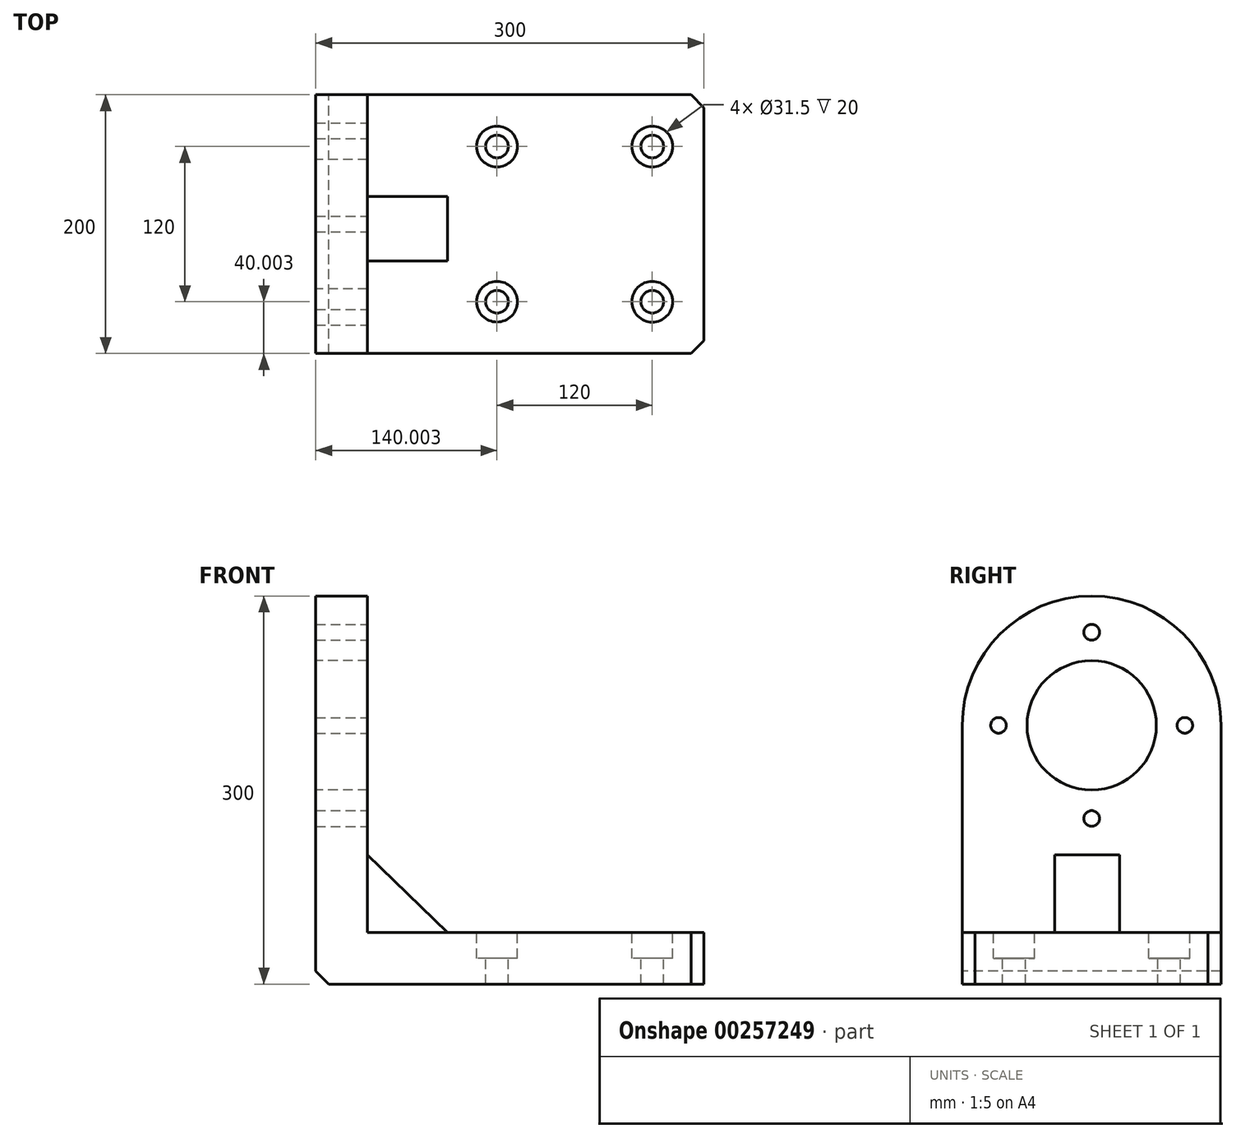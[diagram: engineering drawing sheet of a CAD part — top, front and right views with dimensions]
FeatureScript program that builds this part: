
annotation { "Feature Type Name" : "Feature", "Feature Type Description" : "" }
export const myFeature = defineFeature(function(context is Context, id is Id, definition is map)
    precondition{}
    {
        {
            var Q0;
            Q0=qCreatedBy(makeId("Top.planeOp"),FACE);
            var sketch = newSketch(context, id + "F0", { "sketchPlane" : qUnion([Q0])});
            skLineSegment(sketch, "E0.bottom", {"start": v(-159.08, 103.5) * mm, "end": v(140.92, 103.5) * mm});
            skLineSegment(sketch, "E0.top", {"start": v(-159.08, -96.5) * mm, "end": v(140.92, -96.5) * mm});
            skLineSegment(sketch, "E0.left", {"start": v(-159.08, 103.5) * mm, "end": v(-159.08, -96.5) * mm});
            skLineSegment(sketch, "E0.right", {"start": v(140.92, 103.5) * mm, "end": v(140.92, -96.5) * mm});
            skSolve(sketch);
        }
        {
            var Q0;
            Q0 = qSketchRegion(id + "F0", true);
            extrude(context, id + "F1", {"entities" : qUnion([Q0]), "depth" : 40 * mm});
        }
        {
            var Q0;
            Q0=makeQuery(id+"F1.opExtrude","CAP_FACE",FACE,{"disambiguationData":[OSD([sQuery(id+"F0.wireOp",EDGE,"E0.bottom"),sQuery(id+"F0.wireOp",EDGE,"E0.top"),sQuery(id+"F0.wireOp",EDGE,"E0.left"),sQuery(id+"F0.wireOp",EDGE,"E0.right")])],"isStart":false});
            var sketch = newSketch(context, id + "F2", { "sketchPlane" : qUnion([Q0])});
            skCircle(sketch, "E1", {"center": v(100.92, 63.5) * mm, "radius": 15.75 * mm});
            skCircle(sketch, "E2", {"center": v(100.92, -56.5) * mm, "radius": 15.75 * mm});
            skCircle(sketch, "E3", {"center": v(-19.08, 63.5) * mm, "radius": 15.75 * mm});
            skCircle(sketch, "E4", {"center": v(-19.08, -56.5) * mm, "radius": 15.75 * mm});
            skSolve(sketch);
        }
        {
            var Q0;
            Q0 = qSketchRegion(id + "F2", true);
            extrude(context, id + "F3", {"entities" : qUnion([Q0]), "operationType" : NewBodyOperationType.REMOVE, "oppositeDirection" : true, "depth" : 20 * mm});
        }
        {
            var Q0;
            Q0=makeQuery(id+"F1.opExtrude","CAP_FACE",FACE,{"disambiguationData":[OSD([sQuery(id+"F0.wireOp",EDGE,"E0.bottom"),sQuery(id+"F0.wireOp",EDGE,"E0.top"),sQuery(id+"F0.wireOp",EDGE,"E0.left"),sQuery(id+"F0.wireOp",EDGE,"E0.right")])],"isStart":false});
            var sketch = newSketch(context, id + "F4", { "sketchPlane" : qUnion([Q0])});
            skCircle(sketch, "E5", {"center": v(-19.08, 63.5) * mm, "radius": 8.75 * mm});
            skCircle(sketch, "E6", {"center": v(100.92, 63.5) * mm, "radius": 8.75 * mm});
            skCircle(sketch, "E7", {"center": v(-19.08, -56.5) * mm, "radius": 8.75 * mm});
            skCircle(sketch, "E8", {"center": v(100.92, -56.5) * mm, "radius": 8.75 * mm});
            skSolve(sketch);
        }
        {
            var Q0;
            Q0 = qSketchRegion(id + "F4", true);
            extrude(context, id + "F5", {"entities" : qUnion([Q0]), "operationType" : NewBodyOperationType.REMOVE, "endBound" : BoundingType.THROUGH_ALL, "oppositeDirection" : true, "depth" : 25.4 * mm});
        }
        {
            var Q0;
            Q0=makeQuery(id+"F1.opExtrude","CAP_FACE",FACE,{"disambiguationData":[OSD([sQuery(id+"F0.wireOp",EDGE,"E0.bottom"),sQuery(id+"F0.wireOp",EDGE,"E0.top"),sQuery(id+"F0.wireOp",EDGE,"E0.left"),sQuery(id+"F0.wireOp",EDGE,"E0.right")])],"isStart":false});
            var sketch = newSketch(context, id + "F6", { "sketchPlane" : qUnion([Q0])});
            skLineSegment(sketch, "E9.bottom", {"start": v(-159.08, 103.5) * mm, "end": v(-119.08, 103.5) * mm});
            skLineSegment(sketch, "E9.top", {"start": v(-159.08, -96.5) * mm, "end": v(-119.08, -96.5) * mm});
            skLineSegment(sketch, "E9.left", {"start": v(-159.08, 103.5) * mm, "end": v(-159.08, -96.5) * mm});
            skLineSegment(sketch, "E9.right", {"start": v(-119.08, 103.5) * mm, "end": v(-119.08, -96.5) * mm});
            skSolve(sketch);
        }
        {
            var Q0;
            Q0 = qSketchRegion(id + "F6", true);
            extrude(context, id + "F7", {"entities" : qUnion([Q0]), "operationType" : NewBodyOperationType.ADD, "depth" : 260 * mm});
        }
        {
            var Q0;
            Q0=makeQuery(id+"F7.boolean.opBoolean","MERGE",FACE,{"derivedFrom":[makeQuery(id+"F1.opExtrude","SWEPT_FACE",FACE,{"disambiguationData":[OSD([sQuery(id+"F0.wireOp",EDGE,"E0.left")])]}),makeQuery(id+"F7.opExtrude","SWEPT_FACE",FACE,{"disambiguationData":[OSD([sQuery(id+"F6.wireOp",EDGE,"E9.left")])]})]});
            var sketch = newSketch(context, id + "F8", { "sketchPlane" : qUnion([Q0])});
            skCircle(sketch, "E10", {"center": v(-3.5, 200) * mm, "radius": 100 * mm});
            skPoint(sketch, "E10.centerSnap0", {"position": v(-3.5, 300) * mm});
            skCircle(sketch, "E11", {"center": v(-3.5, 200) * mm, "radius": 50 * mm});
            skSolve(sketch);
        }
        {
            var Q0;
            Q0=makeQuery(id+"F8.imprint","IMPRINT",FACE,{"disambiguationData":[TD([[makeQuery(id+"F8.imprint","IMPRINT",EDGE,{"derivedFrom":sQuery(id+"F8.wireOp",EDGE,"E11")}),1.0]])]});
            var Q1;
            {var subQ0=sQuery(id+"F8.wireOp",EDGE,"E10");var subQ1=sQuery(id+"F6.wireOp",EDGE,"E9.left");var subQ2=makeQuery(id+"F7.opExtrude","CAP_EDGE",EDGE,{"disambiguationData":[OSD([subQ1])],"isStart":false});var subQ3=makeQuery(id+"F8.imprint","INTERSECT",VERTEX,{"derivedFrom":[subQ2,subQ0]});Q1=makeQuery(id+"F8.imprint","IMPRINT",FACE,{"disambiguationData":[TD([[makeQuery(id+"F8.imprint","IMPRINT",EDGE,{"disambiguationData":[TD([[subQ3,1.0]])],"derivedFrom":subQ0}),-1.0]])]});}
            var Q2;
            {var subQ0=sQuery(id+"F8.wireOp",EDGE,"E10");var subQ1=sQuery(id+"F6.wireOp",EDGE,"E9.left");var subQ2=makeQuery(id+"F7.opExtrude","CAP_EDGE",EDGE,{"disambiguationData":[OSD([subQ1])],"isStart":false});var subQ3=makeQuery(id+"F8.imprint","INTERSECT",VERTEX,{"derivedFrom":[subQ2,subQ0]});Q2=makeQuery(id+"F8.imprint","IMPRINT",FACE,{"disambiguationData":[TD([[makeQuery(id+"F8.imprint","IMPRINT",EDGE,{"disambiguationData":[TD([[subQ3,-1.0]])],"derivedFrom":subQ0}),-1.0]])]});}
            extrude(context, id + "F9", {"entities" : qUnion([Q0, Q1, Q2]), "operationType" : NewBodyOperationType.REMOVE, "endBound" : BoundingType.THROUGH_ALL, "oppositeDirection" : true, "depth" : 25.4 * mm});
        }
        {
            var Q0;
            Q0=makeQuery(id+"F7.opExtrude","SWEPT_FACE",FACE,{"disambiguationData":[OSD([sQuery(id+"F6.wireOp",EDGE,"E9.right")])]});
            var sketch = newSketch(context, id + "F10", { "sketchPlane" : qUnion([Q0])});
            skCircle(sketch, "E12", {"center": v(3.5, 200) * mm, "radius": 72 * mm, "construction": true});
            skPoint(sketch, "E13", {"position": v(3.5, 272) * mm});
            skPoint(sketch, "E14", {"position": v(-68.5, 200) * mm});
            skPoint(sketch, "E15", {"position": v(75.5, 200) * mm});
            skPoint(sketch, "E16", {"position": v(3.5, 128) * mm});
            skSolve(sketch);
        }
        {
            var Q0;
            Q0=sQuery(id+"F10.wireOp",VERTEX,"E13");
            var Q1;
            Q1=sQuery(id+"F10.wireOp",VERTEX,"E15");
            var Q2;
            Q2=sQuery(id+"F10.wireOp",VERTEX,"E16");
            var Q3;
            Q3=sQuery(id+"F10.wireOp",VERTEX,"E14");
            var Q4;
            Q4=makeQuery(id+"F1.opExtrude","SWEPT_BODY",BODY,{"disambiguationData":[OSD([sQuery(id+"F0.wireOp",EDGE,"E0.bottom"),sQuery(id+"F0.wireOp",EDGE,"E0.top"),sQuery(id+"F0.wireOp",EDGE,"E0.left"),sQuery(id+"F0.wireOp",EDGE,"E0.right")])]});
            hole(context, id + "F11", {"style" : HoleStyle.SIMPLE, "endStyle" : HoleEndStyle.THROUGH, "standardTappedOrClearance" : lookupTablePath({ "standard" : "ISO", "engagement" : "75%", "pitch" : "2 mm", "size" : "M14", "type" : "Tapped" }), "standardBlindInLast" : lookupTablePath({ "standard" : "ISO", "engagement" : "75%", "pitch" : "2 mm", "size" : "M14", "type" : "Tapped" }), "holeDiameter" : 12.1 * mm, "showTappedDepth" : true, "tappedDepth" : 12.7 * mm, "tapClearance" : 3, "locations" : qUnion([Q0, Q1, Q2, Q3]), "scope" : qUnion([Q4]), "majorDiameter" : 14 * mm});
        }
        {
            var Q0;
            Q0=makeQuery(id+"F1.opExtrude","SWEPT_EDGE",EDGE,{"disambiguationData":[OSD([sQuery(id+"F0.wireOp",EDGE,"E0.top"),sQuery(id+"F0.wireOp",EDGE,"E0.right")])]});
            var Q1;
            Q1=makeQuery(id+"F1.opExtrude","SWEPT_EDGE",EDGE,{"disambiguationData":[OSD([sQuery(id+"F0.wireOp",EDGE,"E0.bottom"),sQuery(id+"F0.wireOp",EDGE,"E0.right")])]});
            var Q2;
            Q2=makeQuery(id+"F1.opExtrude","CAP_EDGE",EDGE,{"disambiguationData":[OSD([sQuery(id+"F0.wireOp",EDGE,"E0.left")])],"isStart":true});
            chamfer(context, id + "F12", {"entities" : qUnion([Q0, Q1, Q2]), "width" : 10 * mm, "tangentPropagation" : true});
        }
        {
            var Q0;
            Q0=qCreatedBy(makeId("Front.planeOp"),FACE);
            var sketch = newSketch(context, id + "F13", { "sketchPlane" : qUnion([Q0])});
            skLineSegment(sketch, "E17.0", {"start": v(-119.08, 40) * mm, "end": v(130.92, 40) * mm});
            skLineSegment(sketch, "E18.0", {"start": v(-119.08, 200) * mm, "end": v(-119.08, 40) * mm});
            skLineSegment(sketch, "E19", {"start": v(-57.32, 40) * mm, "end": v(-119.08, 100) * mm});
            skSolve(sketch);
        }
        {
            var Q0;
            Q0 = qSketchRegion(id + "F13", true);
            extrude(context, id + "F14", {"entities" : qUnion([Q0]), "operationType" : NewBodyOperationType.ADD, "depth" : 25 * mm, "hasSecondDirection" : true, "secondDirectionOppositeDirection" : true, "secondDirectionDepth" : 25 * mm});
        }
    });
